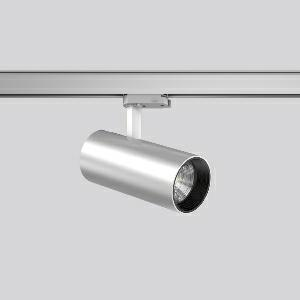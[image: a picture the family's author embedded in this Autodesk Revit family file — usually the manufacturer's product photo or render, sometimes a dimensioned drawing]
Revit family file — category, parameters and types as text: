
# Revit family: deecos_s_mini_742208_004_1_3644
name_source: partatom
category: Lighting Fixtures
units: mm (PartAtom-declared; Revit-internal decimal feet)

## family parameters
Cut with Voids When Loaded = No
Host = Face
Light Source = No
Part Type = Normal
Room Calculation Point = No
Round Connector Dimension = Use Diameter
Shared = No

## types (1)
- DEECOS S mini (1 x LED Modul 940, 3000 lm, 4000)
    Apparent Load = 29 VA
    Approval mark = CE
    CIE Flux Codes = 98 100 100 100 100
    Color Rendering = 92
    Color Temperature = 4000
    Default Elevation = 1800 mm
    Description = Series: DEECOS S mini
LED surface-mounted projector in modern design with no visible cooling ribs. Housing: die-cast aluminium, powder-coated. Rotation range: 356°. Swivel range: 90°. Black plastic ring and recessed LED to prevent glare from the side. Optical assembly with lens made of plastic (polycarbonate) for the best homogeneous light distribution - can be changed without tools. Best colour rendering index Ra>90. With multi adaptor for 3-circuit tracks 230 V. Suitable for Track on ceiling, Wall track. High quality converter without flickering and stroboscopic effect. The following accessories can be mounted without use of tools: interchangeable lenses, decorative glasses, honeycomb louvre, clear and frosted diffusers, white interchangeable plastic ring. 
Colour: silver
Diameter: 87 mm
Height: 214 mm
Lamp: LED
Socket: without socket
Colour temperature: 4000K
Colour rendering index (CRI): 92
System power: 29 W
Rated luminous flux: 3000 lm
Luminous efficiency: 103 lm/W
Control gear: Regulated power supply
Protection class: I
Type of protection: IP 20
    Height = 214 mm
    Lamp = 1 x LED Modul 940
    Lamp Light Flux = 3000 lm
    Lamp count = 1
    Length = 87 mm
    Lifetime = 50000 h
    Luminous efficacy = 103 lm/W
    Manufacturer = RZB
    ModVariant = No
    Model = 742208.004.1
    Mounting Place = Ceiling
    Mounting Type = Rail mounted
    Number of Poles = 1
    OnlyDefault = Yes
    Power Factor = 1
    Product Name = DEECOS S mini
    Product group = Track mounted projectors
    ProductGroupID = 301
    Protection Class = Protection class I
    Protection Degree = IP 20
    RLX_Detail_Level = 1
    RLX_Emergency_Light_Flux = 0 lm
    RLX_Emergency_Type = 0
    RLX_Emergency_Type_DB = No
    RlxData = <blob elided: 37625 chars, md5=07a0929f>
    Socket = socket
    Standby Power = 0 W
    System Light Flux = 3000 lm
    System Power = 29 W
    Type Comments = Product without accessories
    Type Image = 741930.004.jpg
    URL = http://relux.com
    VarID = ---
    Voltage = 230 V
    Voltage Range = 220-240 V
    Weight = 0.00 kg
    Width = 0 mm  [stored 0 ft]

note: [stored X ft] marks values corroborated as IEEE doubles in the binary element streams (Revit-internal decimal feet)

## geometry (parser evidence)
native form markers: Blend x4, Sweep x13
no freeform markers — native parametric forms only
